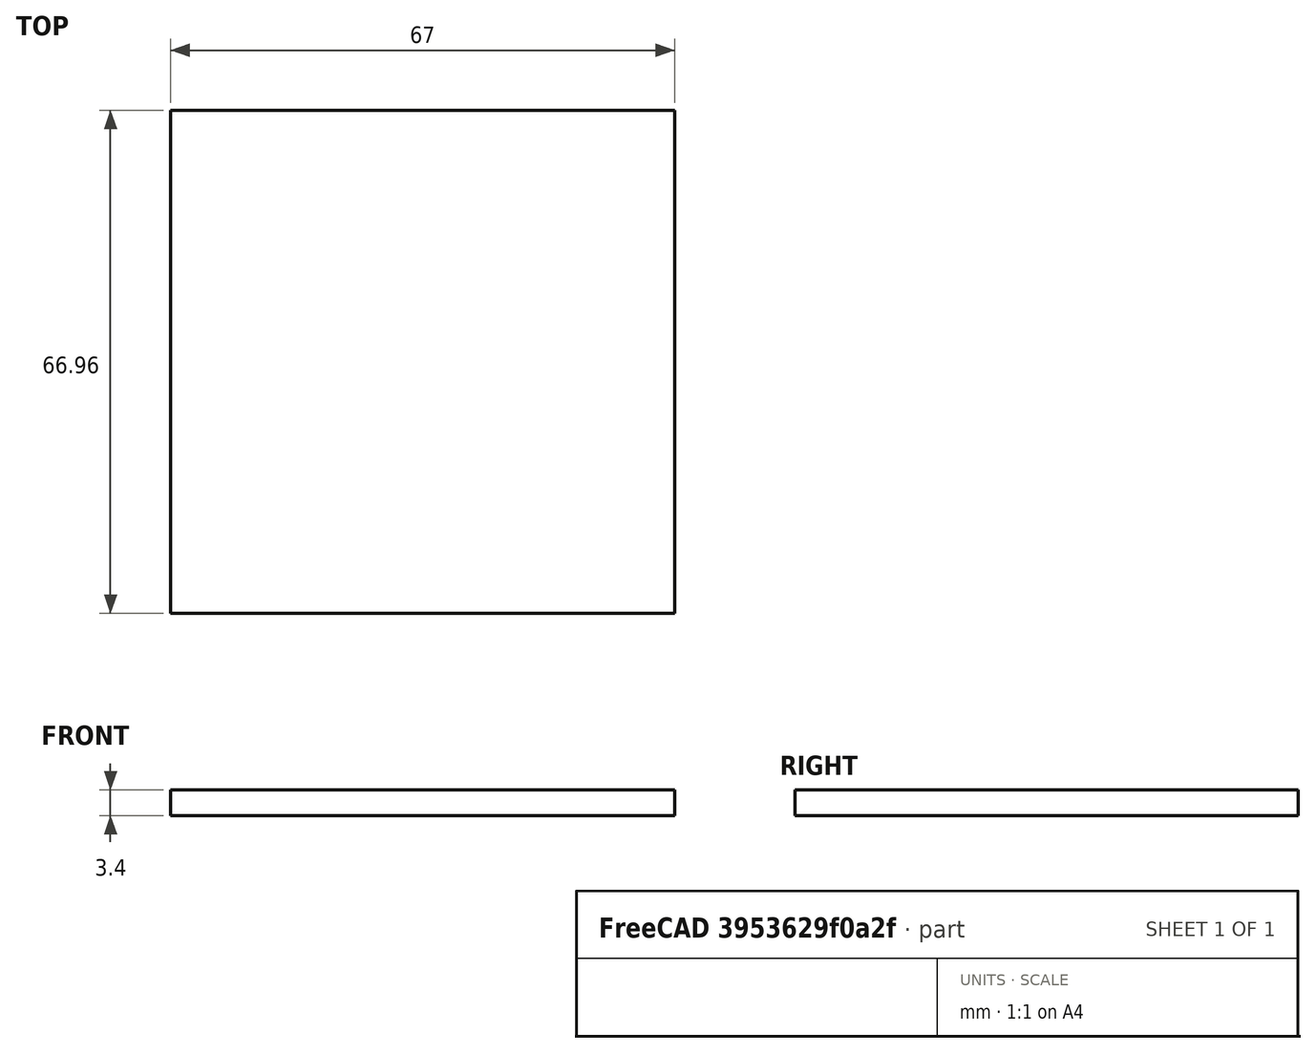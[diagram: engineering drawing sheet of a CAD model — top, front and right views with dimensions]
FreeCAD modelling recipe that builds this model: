
FCSTD DOCUMENT  (FreeCAD 0.17R12703 (Git))
Label: Elektronikspant
License: All rights reserved
LicenseURL: http://en.wikipedia.org/wiki/All_rights_reserved
objects: Path::FeaturePython×10, Part::FeaturePython×2, Part::Feature×1, App::FeaturePython×1, Path::FeatureCompoundPython×1
note: 7 computed .brp shape members not serialized (recipe doc carries the construction recipe); baked Part::Feature solids carry a one-line shape summary decoded from their .brp

FEATURE [Part::Feature] Part__Feature  label="Elektronikspant"
  Placement = pos=(0,0,-3.4) rot=(0,0,1;0rad)
  shape: bbox 67 x 66.96 x 3.4 mm, 25 faces (baked)
FEATURE [App::FeaturePython] SetupSheet  # Path/CAM operation (typed FeaturePython)
  ClearanceHeightExpression = StartDepth+SetupSheet.ClearanceHeightOffset
  ClearanceHeightOffset = 5
  FinalDepthExpression = OpFinalDepth
  HorizRapid = 0
  SafeHeightExpression = StartDepth+SetupSheet.SafeHeightOffset
  SafeHeightOffset = 3
  StartDepthExpression = OpStartDepth
  StepDownExpression = OpToolDiameter
  VertRapid = 0
FEATURE [Part::FeaturePython] Clone  label="Base-Elektronikspant"  # Draft clone (typed FeaturePython)
  AttacherType = Attacher::AttachEngine3D
  Fuse = false
  Objects = -> [Part__Feature]
  PathResource = Base
  Placement = pos=(0,0,-3.4) rot=(0,0,1;0rad)
  Scale = (1,1,1)
FEATURE [Path::FeaturePython] T1__Schaftfraeser_D2  label="T1: Schaftfraeser_D2"  # Path/CAM operation (typed FeaturePython)
  HorizFeed = 400
  HorizRapid = 0
  SpindleDir = 0
  SpindleSpeed = 0
  ToolNumber = 1
  VertFeed = 100
  VertRapid = 0
  expr: VertRapid = SetupSheet.VertRapid
  expr: HorizRapid = SetupSheet.HorizRapid
FEATURE [Part::FeaturePython] Stock  # WARN: FeaturePython — macro-defined, semantics opaque (R4)
  Base = -> Part__Feature
  ExtXneg = 0
  ExtXpos = 0
  ExtYneg = 0
  ExtYpos = 0
  ExtZneg = 0
  ExtZpos = 0
  StockType = FromBase
FEATURE [Path::FeaturePython] Pocket_Shape  # Path/CAM operation (typed FeaturePython)
  Active = true
  AreaParams:
    OpenMode = 0
    Angle = 45.0
    MinArcPoints = 4
    Coplanar = 0
    Tolerance = 1e-07
    CleanDistance = 0.0
    PocketExtraOffset = 0.0
    AngleShift = 0.0
    SubjectFill = 0
    RoundPreceision = 0.0
    Simplify = False
    SectionTolerance = 1e-06
    MaxArcPoints = 100
    SectionOffset = 0.0
    Offset = 0.0
    Accuracy = 0.01
    PocketStepover = 1.6
    ClipFill = 0
    ToolRadius = 1.0
    Outline = False
    ClipperScale = 10000000.0
    FromCenter = True
    Explode = False
    EndType = 0
    Shift = 0.0
    ExtraPass = 0
    Project = False
    JoinType = 0
    Thicken = False
    Stepdown = 1.0
    SectionMode = 2
    MiterLimit = 2.0
    Deflection = 0.01
    Reorient = True
    FitArcs = True
    SectionCount = -1
    PocketMode = 2
    Stepover = 0.0
    Unit = 1.0
    Fill = 0
  Base = -> [Clone]
  ClearanceHeight = 5
  CutMode = 1
  ExtraOffset = 0
  FinalDepth = -1
  FinishDepth = 0
  KeepToolDown = true
  MinTravel = false
  OffsetPattern = 1
  OpFinalDepth = -1
  OpStartDepth = 0
  OpToolDiameter = 2
  PathParams = {'resume_height': 3.0, 'feedrate': 400.0, 'verbose': True, 'orientation': 0, 'return_end': True, 'threshold': 2.001, 'preamble': False, 'retraction': 5.0, 'feedrate_v': 100.0}
  SafeHeight = 3
  StartAt = 0
  StartDepth = 0
  StartPoint = (0,0,0)
  StepDown = 2
  StepOver = 80
  ToolController = -> T1__Schaftfraeser_D2
  UseStartPoint = false
  ZigZagAngle = 45
  expr: ClearanceHeight = StartDepth + SetupSheet.ClearanceHeightOffset
  expr: SafeHeight = StartDepth + SetupSheet.SafeHeightOffset
  expr: StepDown = OpToolDiameter
  expr: FinalDepth = OpFinalDepth
  expr: StartDepth = OpStartDepth
FEATURE [Path::FeaturePython] Profile_Faces  # Path/CAM operation (typed FeaturePython)
  Active = true
  AreaParams:
    OpenMode = 0
    Angle = 45.0
    MinArcPoints = 4
    Coplanar = 0
    Tolerance = 1e-07
    CleanDistance = 0.0
    PocketExtraOffset = 0.0
    AngleShift = 0.0
    SubjectFill = 0
    RoundPreceision = 0.0
    Simplify = False
    SectionTolerance = 1e-06
    MaxArcPoints = 100
    SectionOffset = 0.0
    Offset = -1.0
    Accuracy = 0.01
    PocketStepover = 0.0
    ClipFill = 0
    ToolRadius = 1.0
    Outline = False
    ClipperScale = 10000000.0
    FromCenter = False
    Explode = False
    EndType = 0
    Shift = 0.0
    ExtraPass = 0
    Project = False
    JoinType = 0
    Thicken = False
    Stepdown = 1.0
    SectionMode = 2
    MiterLimit = 2.0
    Deflection = 0.01
    Reorient = True
    FitArcs = True
    SectionCount = -1
    PocketMode = 0
    Stepover = 0.0
    Unit = 1.0
    Fill = 0
  Base = -> [Clone]
  ClearanceHeight = 5
  Direction = 0
  FinalDepth = -1
  JoinType = 0
  MiterLimit = 0.1
  OffsetExtra = 0
  OpFinalDepth = -1
  OpStartDepth = 0
  OpToolDiameter = 2
  PathParams = {'resume_height': 3.0, 'feedrate': 400.0, 'verbose': True, 'orientation': 1, 'return_end': True, 'preamble': False, 'retraction': 5.0, 'feedrate_v': 100.0}
  SafeHeight = 3
  Side = 1
  StartDepth = 0
  StartPoint = (0,0,0)
  StepDown = 2
  ToolController = -> T1__Schaftfraeser_D2
  UseComp = true
  UseStartPoint = false
  processCircles = false
  processHoles = false
  processPerimeter = true
  expr: ClearanceHeight = StartDepth + SetupSheet.ClearanceHeightOffset
  expr: SafeHeight = StartDepth + SetupSheet.SafeHeightOffset
  expr: StepDown = OpToolDiameter
  expr: FinalDepth = OpFinalDepth
  expr: StartDepth = OpStartDepth
FEATURE [Path::FeaturePython] DogboneDressup  # Path/CAM operation (typed FeaturePython)
  Base = -> Profile_Faces
  Custom = 0
  Incision = 0
  Side = 0
  Style = 0
  ToolController = -> T1__Schaftfraeser_D2
FEATURE [Path::FeaturePython] Profile_Faces001  # Path/CAM operation (typed FeaturePython)
  Active = true
  AreaParams:
    OpenMode = 0
    Angle = 45.0
    MinArcPoints = 4
    Coplanar = 0
    Tolerance = 1e-07
    CleanDistance = 0.0
    PocketExtraOffset = 0.0
    AngleShift = 0.0
    SubjectFill = 0
    RoundPreceision = 0.0
    Simplify = False
    SectionTolerance = 1e-06
    MaxArcPoints = 100
    SectionOffset = 0.0
    Offset = -1.0
    Accuracy = 0.01
    PocketStepover = 0.0
    ClipFill = 0
    ToolRadius = 1.0
    Outline = False
    ClipperScale = 10000000.0
    FromCenter = False
    Explode = False
    EndType = 0
    Shift = 0.0
    ExtraPass = 0
    Project = False
    JoinType = 0
    Thicken = False
    Stepdown = 1.0
    SectionMode = 2
    MiterLimit = 2.0
    Deflection = 0.01
    Reorient = True
    FitArcs = True
    SectionCount = -1
    PocketMode = 0
    Stepover = 0.0
    Unit = 1.0
    Fill = 0
  Base = -> [Clone]
  ClearanceHeight = 5
  Direction = 0
  FinalDepth = -3.7
  JoinType = 0
  MiterLimit = 0.1
  OffsetExtra = 0
  OpFinalDepth = -3.4
  OpStartDepth = 0
  OpToolDiameter = 2
  PathParams = {'resume_height': 3.0, 'feedrate': 400.0, 'verbose': True, 'orientation': 1, 'return_end': True, 'preamble': False, 'retraction': 5.0, 'feedrate_v': 100.0}
  SafeHeight = 3
  Side = 1
  StartDepth = 0
  StartPoint = (0,0,0)
  StepDown = 2
  ToolController = -> T1__Schaftfraeser_D2
  UseComp = true
  UseStartPoint = false
  processCircles = false
  processHoles = false
  processPerimeter = true
  expr: ClearanceHeight = StartDepth + SetupSheet.ClearanceHeightOffset
  expr: SafeHeight = StartDepth + SetupSheet.SafeHeightOffset
  expr: StepDown = 2
  expr: FinalDepth = -3.7000000000000002
  expr: StartDepth = OpStartDepth
FEATURE [Path::FeaturePython] DogboneDressup001  # Path/CAM operation (typed FeaturePython)
  Base = -> Profile_Faces001
  Custom = 0
  Incision = 0
  Side = 0
  Style = 0
  ToolController = -> T1__Schaftfraeser_D2
FEATURE [Path::FeaturePython] Contour  # Path/CAM operation (typed FeaturePython)
  Active = true
  AreaParams:
    OpenMode = 0
    Angle = 45.0
    MinArcPoints = 4
    Coplanar = 2
    Tolerance = 1e-07
    CleanDistance = 0.0
    PocketExtraOffset = 0.0
    AngleShift = 0.0
    SubjectFill = 0
    RoundPreceision = 0.0
    Simplify = False
    SectionTolerance = 1e-06
    MaxArcPoints = 100
    SectionOffset = 0.0
    Offset = 1.0
    Accuracy = 0.01
    PocketStepover = 0.0
    ClipFill = 0
    ToolRadius = 1.0
    Outline = False
    ClipperScale = 10000000.0
    FromCenter = False
    Explode = False
    EndType = 0
    Shift = 0.0
    ExtraPass = 0
    Project = False
    JoinType = 0
    Thicken = False
    Stepdown = 1.0
    SectionMode = 2
    MiterLimit = 2.0
    Deflection = 0.01
    Reorient = True
    FitArcs = True
    SectionCount = -1
    PocketMode = 0
    Stepover = 0.0
    Unit = 1.0
    Fill = 0
  ClearanceHeight = 5
  Direction = 1
  FinalDepth = -3.7
  JoinType = 0
  MiterLimit = 0.1
  OffsetExtra = 0
  OpFinalDepth = -3.4
  OpStartDepth = 0
  OpToolDiameter = 2
  PathParams = {'resume_height': 3.0, 'feedrate': 400.0, 'verbose': True, 'orientation': 0, 'return_end': True, 'preamble': False, 'retraction': 5.0, 'feedrate_v': 100.0}
  SafeHeight = 3
  Side = 0
  StartDepth = 0
  StartPoint = (0,0,0)
  StepDown = 2
  ToolController = -> T1__Schaftfraeser_D2
  UseComp = true
  UseStartPoint = false
  expr: ClearanceHeight = StartDepth + SetupSheet.ClearanceHeightOffset
  expr: SafeHeight = StartDepth + SetupSheet.SafeHeightOffset
  expr: StepDown = 2
  expr: FinalDepth = -3.7000000000000002
  expr: StartDepth = OpStartDepth
FEATURE [Path::FeaturePython] DogboneDressup002  # Path/CAM operation (typed FeaturePython)
  Base = -> Contour
  Custom = 0
  Incision = 0
  Side = 0
  Style = 0
  ToolController = -> T1__Schaftfraeser_D2
FEATURE [Path::FeaturePython] TagDressup  # Path/CAM operation (typed FeaturePython)
  Angle = 45
  Base = -> DogboneDressup002
  Height = 1.6
  Positions = (3) [(-29.8776,17.2499,0),(0.604796,-34.4929,0),(29.2411,18.3081,0)]
  Radius = 0
  SegmentationFactor = 50
  Width = 4
FEATURE [Path::FeatureCompoundPython] Operations  # Path/CAM operation (typed FeaturePython)
  Group = -> [Pocket_Shape,DogboneDressup,DogboneDressup001,TagDressup]
  UsePlacements = false
FEATURE [Path::FeaturePython] Job  # Path/CAM operation (typed FeaturePython)
  Base = -> Clone
  GeometryTolerance = 0.01
  Operations = -> Operations
  PostProcessor = 5
  SetupSheet = -> SetupSheet
  Stock = -> Stock
  ToolController = -> [T1__Schaftfraeser_D2]
